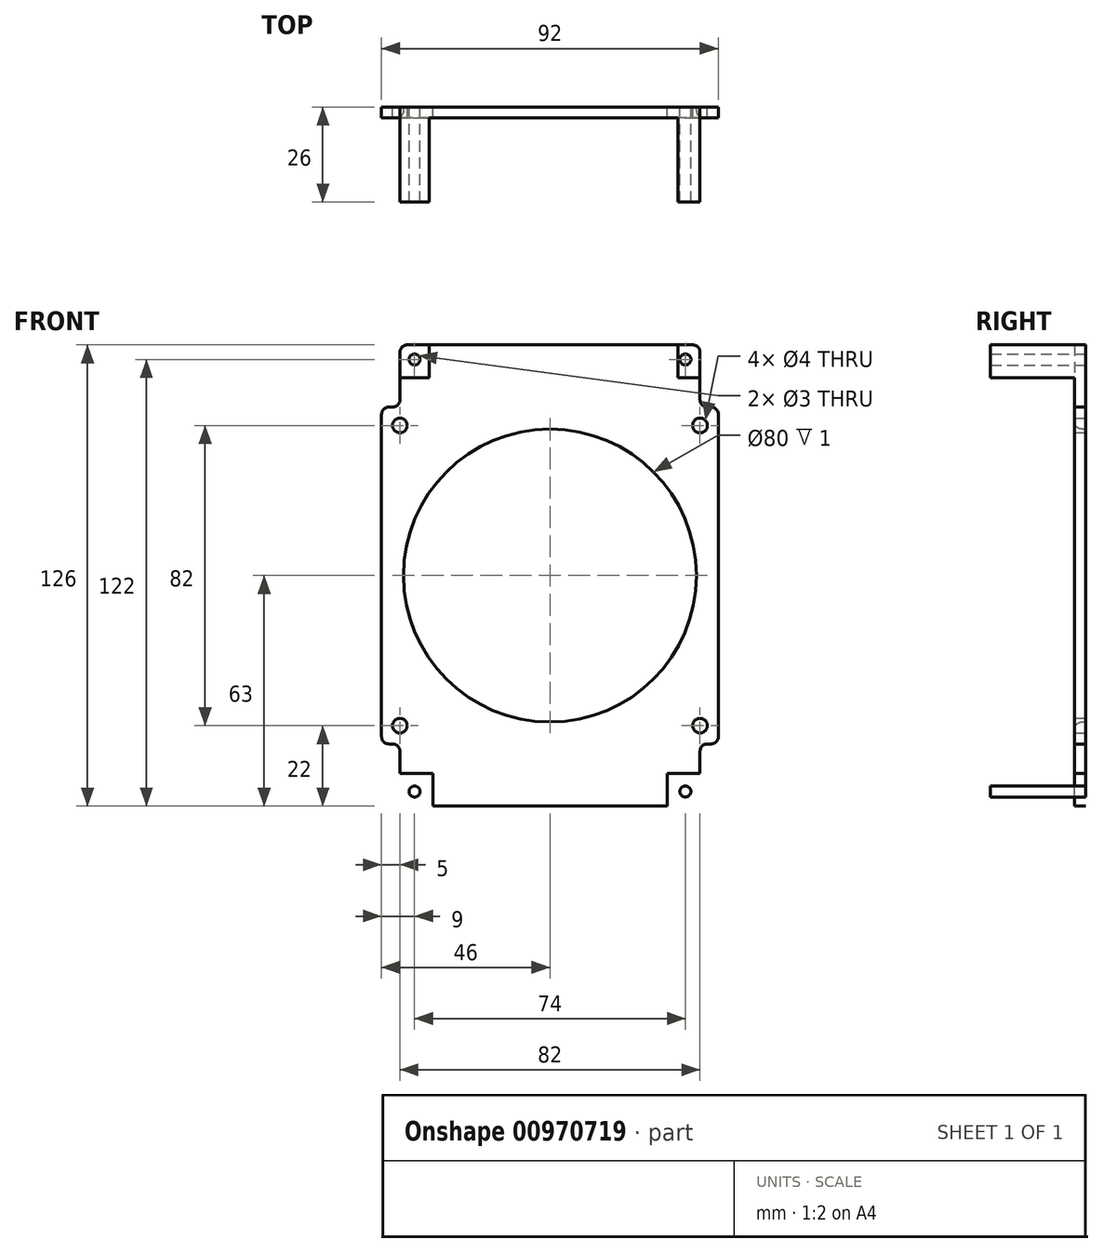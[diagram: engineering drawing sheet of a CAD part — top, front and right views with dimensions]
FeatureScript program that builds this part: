
annotation { "Feature Type Name" : "Feature", "Feature Type Description" : "" }
export const myFeature = defineFeature(function(context is Context, id is Id, definition is map)
    precondition{}
    {
        {
            var Q0;
            Q0=qCreatedBy(makeId("Front.planeOp"),FACE);
            var sketch = newSketch(context, id + "F0", { "sketchPlane" : qUnion([Q0])});
            skPoint(sketch, "E0.middle", {"position": v(0, 0) * mm});
            skCircle(sketch, "E1", {"center": v(-41, 41) * mm, "radius": 2 * mm});
            skCircle(sketch, "E2", {"center": v(41, 41) * mm, "radius": 2 * mm});
            skCircle(sketch, "E3", {"center": v(41, -41) * mm, "radius": 2 * mm});
            skCircle(sketch, "E4", {"center": v(-41, -41) * mm, "radius": 2 * mm});
            skLineSegment(sketch, "E5.bottom", {"start": v(46, -46) * mm, "end": v(-46, -46) * mm});
            skLineSegment(sketch, "E5.top", {"start": v(46, 46) * mm, "end": v(-46, 46) * mm});
            skLineSegment(sketch, "E5.left", {"start": v(46, -46) * mm, "end": v(46, 46) * mm});
            skLineSegment(sketch, "E5.right", {"start": v(-46, -46) * mm, "end": v(-46, 46) * mm});
            skLineSegment(sketch, "E6.bottom", {"start": v(41, 46) * mm, "end": v(-41, 46) * mm});
            skLineSegment(sketch, "E6.top", {"start": v(41, 63) * mm, "end": v(-41, 63) * mm});
            skLineSegment(sketch, "E6.left", {"start": v(41, 46) * mm, "end": v(41, 63) * mm});
            skLineSegment(sketch, "E6.right", {"start": v(-41, 46) * mm, "end": v(-41, 63) * mm});
            skPoint(sketch, "E6.middle", {"position": v(0, 54.5) * mm});
            skLineSegment(sketch, "E7.MirrorCS", {"start": v(-41, -46) * mm, "end": v(-41, -63) * mm});
            skLineSegment(sketch, "E8.MirrorCS", {"start": v(41, -46) * mm, "end": v(-41, -46) * mm});
            skLineSegment(sketch, "E9.MirrorCS", {"start": v(41, -63) * mm, "end": v(-41, -63) * mm});
            skLineSegment(sketch, "E10.MirrorCS", {"start": v(41, -46) * mm, "end": v(41, -63) * mm});
            skCircle(sketch, "E11", {"center": v(-37, 59) * mm, "radius": 1.5 * mm});
            skCircle(sketch, "E12", {"center": v(37, 59) * mm, "radius": 1.5 * mm});
            skCircle(sketch, "E13.MirrorC", {"center": v(37, -59) * mm, "radius": 1.5 * mm});
            skCircle(sketch, "E14.MirrorC", {"center": v(-37, -59) * mm, "radius": 1.5 * mm});
            skLineSegment(sketch, "E15.bottom", {"start": v(-41, 63) * mm, "end": v(-33, 63) * mm});
            skLineSegment(sketch, "E15.top", {"start": v(-41, 54) * mm, "end": v(-33, 54) * mm});
            skLineSegment(sketch, "E15.left", {"start": v(-41, 63) * mm, "end": v(-41, 54) * mm});
            skLineSegment(sketch, "E15.right", {"start": v(-33, 63) * mm, "end": v(-33, 54) * mm});
            skLineSegment(sketch, "E16.bottom", {"start": v(41, 63) * mm, "end": v(35, 63) * mm});
            skLineSegment(sketch, "E16.top", {"start": v(41, 54) * mm, "end": v(35, 54) * mm});
            skLineSegment(sketch, "E16.left", {"start": v(41, 63) * mm, "end": v(41, 54) * mm});
            skLineSegment(sketch, "E16.right", {"start": v(35, 63) * mm, "end": v(35, 54) * mm});
            skLineSegment(sketch, "E17.bottom", {"start": v(41, -63) * mm, "end": v(32, -63) * mm});
            skLineSegment(sketch, "E17.top", {"start": v(41, -54) * mm, "end": v(32, -54) * mm});
            skLineSegment(sketch, "E17.left", {"start": v(41, -63) * mm, "end": v(41, -54) * mm});
            skLineSegment(sketch, "E17.right", {"start": v(32, -63) * mm, "end": v(32, -54) * mm});
            skLineSegment(sketch, "E18.bottom", {"start": v(-41, -63) * mm, "end": v(-32, -63) * mm});
            skLineSegment(sketch, "E18.top", {"start": v(-41, -54) * mm, "end": v(-32, -54) * mm});
            skLineSegment(sketch, "E18.left", {"start": v(-41, -63) * mm, "end": v(-41, -54) * mm});
            skLineSegment(sketch, "E18.right", {"start": v(-32, -63) * mm, "end": v(-32, -54) * mm});
            skCircle(sketch, "E19", {"center": v(0, 0) * mm, "radius": 40 * mm});
            skSolve(sketch);
        }
        {
            var Q0;
            Q0=makeQuery(id+"F0.imprint","IMPRINT",FACE,{"disambiguationData":[TD([[makeQuery(id+"F0.imprint","IMPRINT",EDGE,{"derivedFrom":sQuery(id+"F0.wireOp",EDGE,"E1")}),-1.0]])]});
            var Q1;
            {var subQ6=sQuery(id+"F0.wireOp",EDGE,"E17.top");Q1=makeQuery(id+"F0.imprint","IMPRINT",FACE,{"disambiguationData":[TD([[makeQuery(id+"F0.imprint","IMPRINT",EDGE,{"derivedFrom":subQ6}),-1.0]])]});}
            var Q2;
            {var subQ0=sQuery(id+"F0.wireOp",EDGE,"E15.top");Q2=makeQuery(id+"F0.imprint","IMPRINT",FACE,{"disambiguationData":[TD([[makeQuery(id+"F0.imprint","IMPRINT",EDGE,{"derivedFrom":subQ0}),-1.0]])]});}
            extrude(context, id + "F1", {"entities" : qUnion([Q0, Q1, Q2]), "depth" : 3 * mm, "offsetDistance" : 25 * mm});
        }
        {
            var Q0;
            Q0=makeQuery(id+"F0.imprint","IMPRINT",FACE,{"disambiguationData":[TD([[makeQuery(id+"F0.imprint","IMPRINT",EDGE,{"derivedFrom":sQuery(id+"F0.wireOp",EDGE,"E11")}),-1.0]])]});
            var Q1;
            Q1=makeQuery(id+"F0.imprint","IMPRINT",FACE,{"disambiguationData":[TD([[makeQuery(id+"F0.imprint","IMPRINT",EDGE,{"derivedFrom":sQuery(id+"F0.wireOp",EDGE,"E12")}),-1.0]])]});
            var Q2;
            Q2=makeQuery(id+"F0.imprint","IMPRINT",FACE,{"disambiguationData":[TD([[makeQuery(id+"F0.imprint","IMPRINT",EDGE,{"derivedFrom":sQuery(id+"F0.wireOp",EDGE,"E13.MirrorC")}),1.0]])]});
            var Q3;
            Q3=makeQuery(id+"F0.imprint","IMPRINT",FACE,{"disambiguationData":[TD([[makeQuery(id+"F0.imprint","IMPRINT",EDGE,{"derivedFrom":sQuery(id+"F0.wireOp",EDGE,"E14.MirrorC")}),1.0]])]});
            extrude(context, id + "F2", {"entities" : qUnion([Q0, Q1, Q2, Q3]), "operationType" : NewBodyOperationType.ADD, "depth" : 26 * mm, "offsetDistance" : 25 * mm});
        }
        {
            var Q0;
            Q0=makeQuery(id+"F1.opExtrude","CAP_EDGE",EDGE,{"disambiguationData":[OSD([sQuery(id+"F0.wireOp",EDGE,"E19")])],"isStart":false});
            var Q1;
            Q1=makeQuery(id+"F1.opExtrude","SWEPT_EDGE",EDGE,{"disambiguationData":[OSD([sQuery(id+"F0.wireOp",EDGE,"E5.bottom"),sQuery(id+"F0.wireOp",EDGE,"E5.right")])]});
            var Q2;
            Q2=makeQuery(id+"F1.opExtrude","SWEPT_EDGE",EDGE,{"disambiguationData":[OSD([sQuery(id+"F0.wireOp",EDGE,"E5.top"),sQuery(id+"F0.wireOp",EDGE,"E5.right")])]});
            var Q3;
            Q3=makeQuery(id+"F1.opExtrude","SWEPT_EDGE",EDGE,{"disambiguationData":[OSD([sQuery(id+"F0.wireOp",EDGE,"E5.bottom"),sQuery(id+"F0.wireOp",EDGE,"E5.left")])]});
            var Q4;
            Q4=makeQuery(id+"F1.opExtrude","SWEPT_EDGE",EDGE,{"disambiguationData":[OSD([sQuery(id+"F0.wireOp",EDGE,"E5.bottom"),sQuery(id+"F0.wireOp",EDGE,"E10.MirrorCS")])]});
            var Q5;
            Q5=makeQuery(id+"F1.opExtrude","SWEPT_EDGE",EDGE,{"disambiguationData":[OSD([sQuery(id+"F0.wireOp",EDGE,"E5.bottom"),sQuery(id+"F0.wireOp",EDGE,"E7.MirrorCS")])]});
            var Q6;
            Q6=makeQuery(id+"F2.opExtrude","SWEPT_EDGE",EDGE,{"disambiguationData":[OSD([sQuery(id+"F0.wireOp",EDGE,"E7.MirrorCS"),sQuery(id+"F0.wireOp",EDGE,"E9.MirrorCS")])]});
            var Q7;
            Q7=makeQuery(id+"F2.opExtrude","SWEPT_EDGE",EDGE,{"disambiguationData":[OSD([sQuery(id+"F0.wireOp",EDGE,"E9.MirrorCS"),sQuery(id+"F0.wireOp",EDGE,"E10.MirrorCS")])]});
            var Q8;
            Q8=makeQuery(id+"F1.opExtrude","SWEPT_EDGE",EDGE,{"disambiguationData":[OSD([sQuery(id+"F0.wireOp",EDGE,"E5.top"),sQuery(id+"F0.wireOp",EDGE,"E5.left")])]});
            var Q9;
            Q9=makeQuery(id+"F1.opExtrude","SWEPT_EDGE",EDGE,{"disambiguationData":[OSD([sQuery(id+"F0.wireOp",EDGE,"E5.top"),sQuery(id+"F0.wireOp",EDGE,"E6.left")])]});
            var Q10;
            Q10=makeQuery(id+"F2.opExtrude","SWEPT_EDGE",EDGE,{"disambiguationData":[OSD([sQuery(id+"F0.wireOp",EDGE,"E6.top"),sQuery(id+"F0.wireOp",EDGE,"E6.left")])]});
            var Q11;
            Q11=makeQuery(id+"F2.opExtrude","SWEPT_EDGE",EDGE,{"disambiguationData":[OSD([sQuery(id+"F0.wireOp",EDGE,"E6.top"),sQuery(id+"F0.wireOp",EDGE,"E6.right")])]});
            var Q12;
            Q12=makeQuery(id+"F1.opExtrude","SWEPT_EDGE",EDGE,{"disambiguationData":[OSD([sQuery(id+"F0.wireOp",EDGE,"E5.top"),sQuery(id+"F0.wireOp",EDGE,"E6.right")])]});
            fillet(context, id + "F3", {"entities" : qUnion([Q0, Q1, Q2, Q3, Q4, Q5, Q6, Q7, Q8, Q9, Q10, Q11, Q12]), "radius" : 2 * mm, "tangentPropagation" : true, "allowEdgeOverflow" : false});
        }
    });
